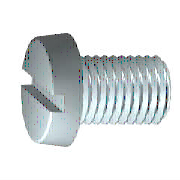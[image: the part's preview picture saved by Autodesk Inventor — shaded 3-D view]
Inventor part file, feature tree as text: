
AUTODESK INVENTOR PART (.ipt)
format: ipt  version: 2022 (Build 260153000, 153)  size: 186,368 bytes
history: native  units: mm (DEFAULTED — no unit token found)
features: sketch x2, other x1, extrude x1, plane x1
ambient origin geometry x7: Origin, YZ Plane, XZ Plane, X Axis, Y Axis, Z Axis, Center Point
bodies: Solid1 (feature_tree)
feature tree (5):
  other  "Базовый элемент"
  sketch  "Эскиз2"
  extrude  "Паз"  Depth=16.0mm
  plane  "Work Plane1"
  sketch  "Эскиз1"
